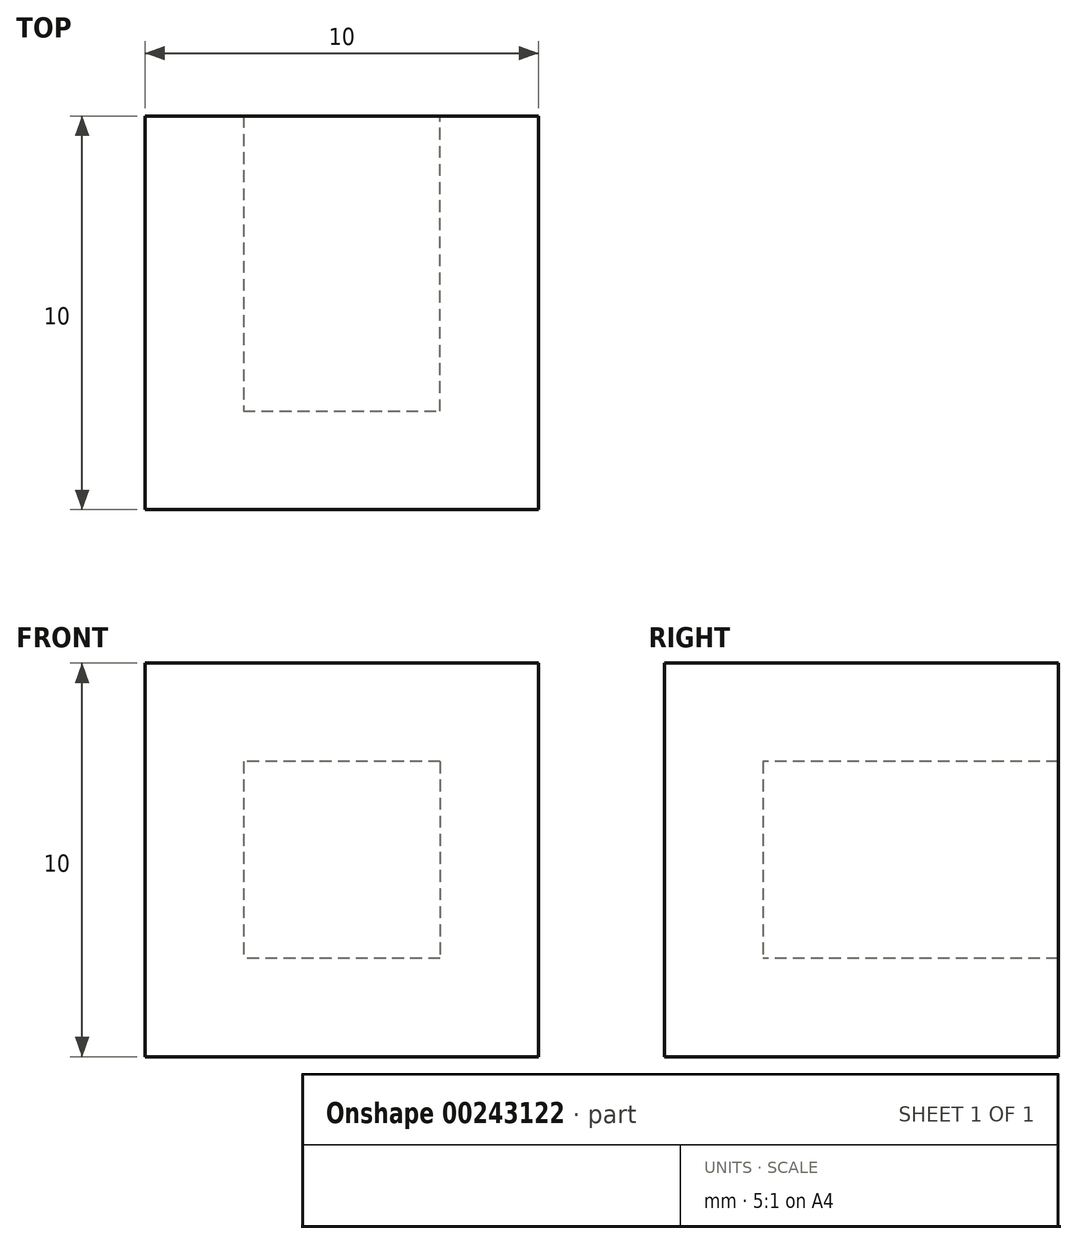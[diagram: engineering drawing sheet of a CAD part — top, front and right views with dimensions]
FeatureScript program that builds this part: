
annotation { "Feature Type Name" : "Feature", "Feature Type Description" : "" }
export const myFeature = defineFeature(function(context is Context, id is Id, definition is map)
    precondition{}
    {
        {
            var Q0;
            Q0=qCreatedBy(makeId("Top.planeOp"),FACE);
            var sketch = newSketch(context, id + "F0", { "sketchPlane" : qUnion([Q0])});
            skLineSegment(sketch, "E0", {"start": v(0, 0) * mm, "end": v(10, 0) * mm});
            skLineSegment(sketch, "E1", {"start": v(10, 0) * mm, "end": v(10, 10) * mm});
            skLineSegment(sketch, "E2", {"start": v(10, 10) * mm, "end": v(0, 10) * mm});
            skLineSegment(sketch, "E3", {"start": v(0, 10) * mm, "end": v(0, 0) * mm});
            skSolve(sketch);
        }
        {
            var Q0;
            Q0 = qSketchRegion(id + "F0", true);
            extrude(context, id + "F1", {"entities" : qUnion([Q0]), "depth" : 10 * mm});
        }
        {
            var Q0;
            Q0=makeQuery(id+"F1.opExtrude","SWEPT_FACE",FACE,{"disambiguationData":[OSD([sQuery(id+"F0.wireOp",EDGE,"E2")])]});
            shell(context, id + "F2", {"entities" : qUnion([Q0]), "thickness" : 2.5 * mm});
        }
    });
